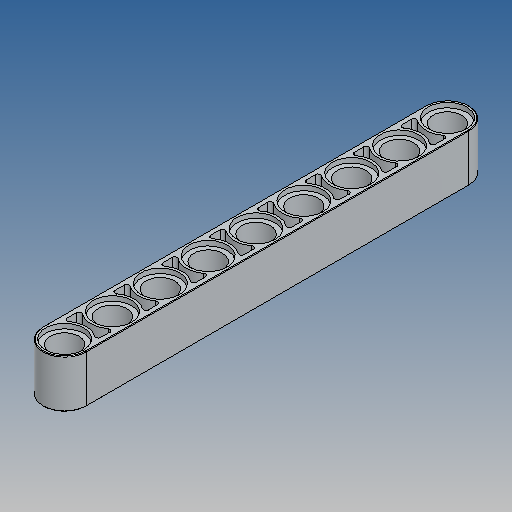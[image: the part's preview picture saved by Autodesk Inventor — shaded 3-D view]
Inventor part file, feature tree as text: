
AUTODESK INVENTOR PART (.ipt)
format: ipt  version: 2025 (Build 290162010, 162A)  size: 471,552 bytes
history: native  units: mm
features: extrude x3, sketch x3, mirror x1, fillet x1
ambient origin geometry x8: Origin, YZ Plane, XZ Plane, XY Plane, X Axis, Y Axis, Z Axis, Center Point
bodies: Solid1 (feature_tree)
feature tree (8):
  extrude  "Extrusion1"  Depth=7.2mm
  sketch  "Sketch6"  dims[d48=64.0mm d49=6.4mm d50=4.8mm d52=0.8mm d53=80.0mm d55=8.0mm d56=10.0mm d58=10.0mm d60=0.4mm d61=0.1mm]
  extrude  "Extrusion7"  Depth=3.1mm TaperAngle=0.0deg
  extrude  "Extrusion8"  Depth=6.4mm
  mirror  "Mirror1"
  fillet  "Fillet2"  Radius=4.8mm
  sketch  "Sketch1"  dims[d14=8.0mm d15=0.0mm d32=7.2mm]
  sketch  "Skizze - Rechteckige Anordnung1"  dims[d41=0.8mm d42=0.0mm d43=3.1mm d44=0.0mm]
